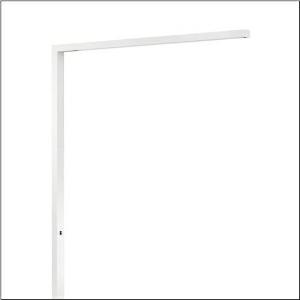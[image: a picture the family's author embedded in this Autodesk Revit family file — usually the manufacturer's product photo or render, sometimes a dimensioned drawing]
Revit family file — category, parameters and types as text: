
# Revit family: silica_r__11_floor_5mx51bs3wzk00002xx_06fb
name_source: partatom
category: Lighting Fixtures
units: mm (PartAtom-declared; Revit-internal decimal feet)

## family parameters
Cut with Voids When Loaded = No
Host = Face
Light Source = No
Part Type = Normal
Room Calculation Point = No
Round Connector Dimension = Use Diameter
Shared = No

## types (1)
- --- (1 x LED, 3960 lm / 8500 lm, 24.4 W / 54.9 W, 4000K)
    Apparent Load = 79 VA
    CIE Flux Codes = 82 97 100 100 100 / - - - 0 100
    Color Rendering = 80
    Color Temperature = 4000K
    Default Elevation = 1800 mm
    Description = Silica® 11 Floor, floorstanding luminaire, of PMMA, primary optical cover: cover panel, of PMMA, light emission: indirect/direct distribution, primary light characteristic: symmetric, installation type: not mounted, LED, rated luminous flux: 12.460lm, luminous efficacy: 157lm/W, light colour: 840, colour temperature: 4000K, control gear: DALI, daylight-dependent control, mains connection: 230V, AC, 50Hz, connection cable pre-assembled, cable length: 3m, rated input power: 79W, luminaire head, rectangular, rounded, of aluminium, coated, traffic white (RAL 9016), supporting column, angular, of aluminium, coated, traffic white (RAL 9016), baseplate, of steel, coated, traffic white (RAL 9016), length: 1.316mm, width: 65mm, protection rating (complete): IP20, insulation class (complete): insulation class I (protective earthing), certification: CE, permissible operating ambient temperature: 0..+35°C, standard: EN 50419, packaging unit: 1 piece
    Height = 40 mm  [stored 0.131234 ft]
    Lamp = 1 x LED
    Lamp Light Flux = 3960 lm / 8500 lm
    Lamp Power = 24.4 W / 54.9 W
    Lamp count = 1
    Length = 1317 mm
    Luminous efficacy = 157 lm/W
    Manufacturer = Siteco
    ModVariant = No
    Model = 5MX51BS3WZK00002XX
    Mounting Place = Floor
    Mounting Type = Freestanding
    Number of Poles = 1
    OnlyDefault = Yes
    Power Factor = 1
    Product Name = Silica® 11 Floor
    Product group = floorstanding luminaire
    ProductGroupID = 1302
    Protection Class = Protection class I
    Protection Degree = IP 20
    RLX_Detail_Level = 1
    RLX_Emergency_Light_Flux = 0 lm
    RLX_Emergency_Type = 0
    RLX_Emergency_Type_DB = No
    RlxData = <blob elided: 18225 chars, md5=337a6677>
    Socket = socket
    Standby Power = 0 W
    System Light Flux = 12460 lm
    System Power = 79 W
    Type Comments = factory setting: direct and indirect light
    Type Image = l_1004655.jpg
    URL = http://relux.com
    VarID = @adj_198499
    Voltage = 0 V
    Weight = 0.00 kg
    Width = 65 mm

note: [stored X ft] marks values corroborated as IEEE doubles in the binary element streams (Revit-internal decimal feet)

## geometry (parser evidence)
native form markers: Blend x4, Sweep x16
no freeform markers — native parametric forms only
